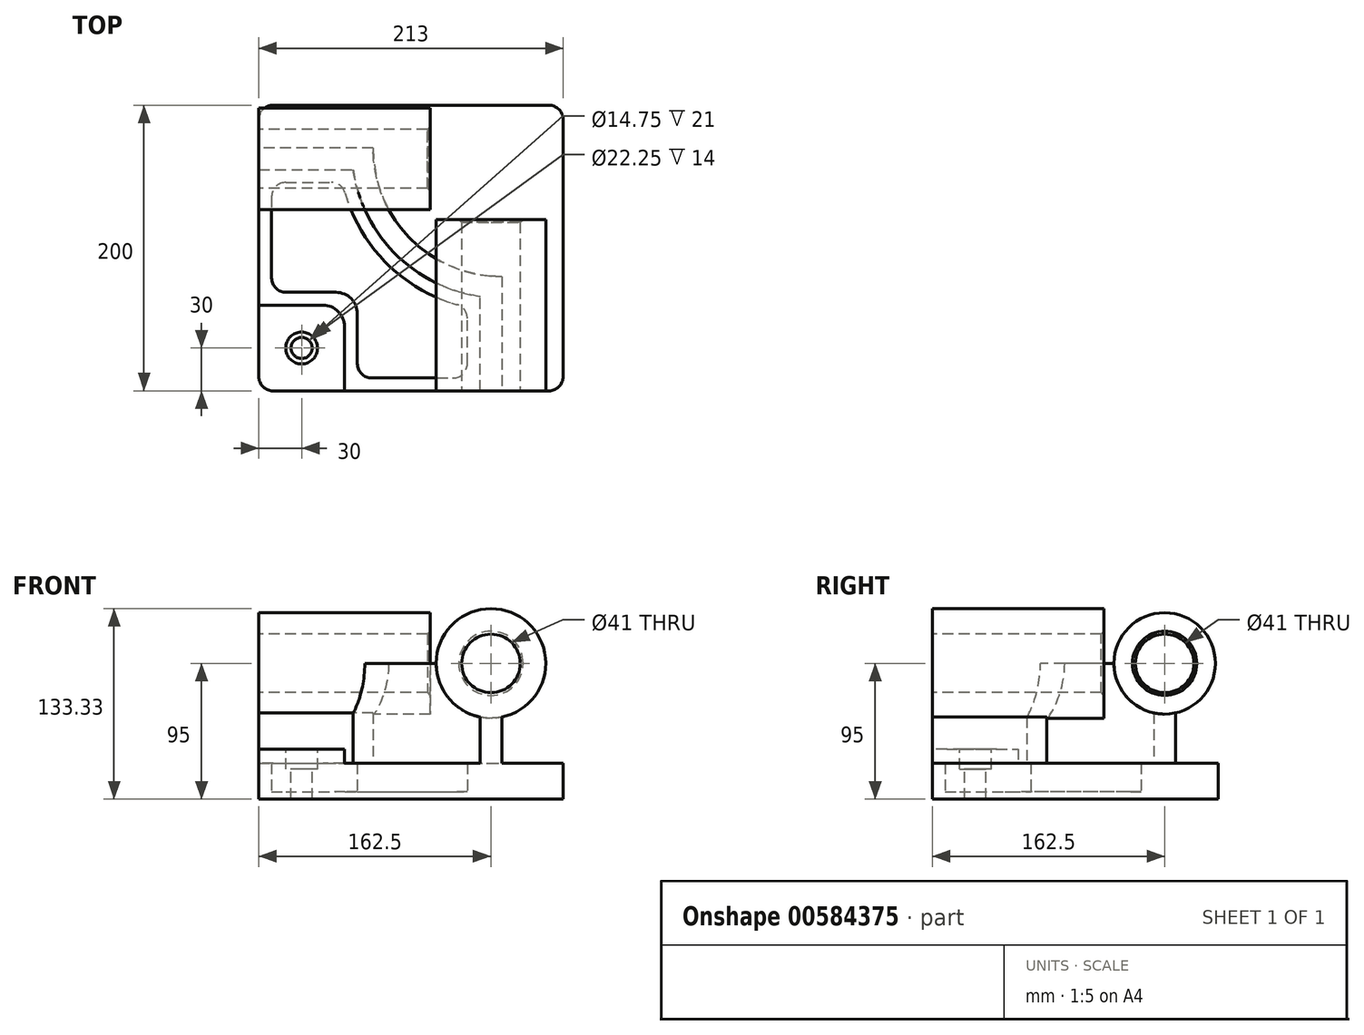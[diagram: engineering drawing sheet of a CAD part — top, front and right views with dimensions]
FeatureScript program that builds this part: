
annotation { "Feature Type Name" : "Feature", "Feature Type Description" : "" }
export const myFeature = defineFeature(function(context is Context, id is Id, definition is map)
    precondition{}
    {
        {
            var Q0;
            Q0=qCreatedBy(makeId("Top.planeOp"),FACE);
            var sketch = newSketch(context, id + "F0", { "sketchPlane" : qUnion([Q0])});
            skLineSegment(sketch, "E0", {"start": v(0, 0) * mm, "end": v(213, 0) * mm});
            skLineSegment(sketch, "E1", {"start": v(0, 0) * mm, "end": v(0, 200) * mm});
            skLineSegment(sketch, "E2", {"start": v(0, 200) * mm, "end": v(213, 200) * mm});
            skLineSegment(sketch, "E3", {"start": v(213, 200) * mm, "end": v(213, 0) * mm});
            skLineSegment(sketch, "E4", {"start": v(0, 170) * mm, "end": v(80, 170) * mm});
            skLineSegment(sketch, "E5", {"start": v(170, 80) * mm, "end": v(170, 0) * mm});
            skLineSegment(sketch, "E6", {"start": v(0, 60) * mm, "end": v(45, 60) * mm});
            skLineSegment(sketch, "E7", {"start": v(60, 45) * mm, "end": v(60, 0) * mm});
            skPoint(sketch, "E8.visualSharp", {"position": v(60, 60) * mm});
            skArc(sketch, "E8.filletArc", {"start": v(60, 45) * mm, "mid": v(55.6, 55.6) * mm, "end": v(45, 60) * mm});
            skArc(sketch, "E9", {"start": v(80, 170) * mm, "mid": v(106.36, 106.36) * mm, "end": v(170, 80) * mm});
            skArc(sketch, "E10", {"start": v(66.08, 155) * mm, "mid": v(95.75, 95.75) * mm, "end": v(155, 66.08) * mm});
            skLineSegment(sketch, "E11", {"start": v(0, 155) * mm, "end": v(66.08, 155) * mm});
            skLineSegment(sketch, "E12", {"start": v(155, 0) * mm, "end": v(155, 66.08) * mm});
            skLineSegment(sketch, "E13", {"start": v(9, 136) * mm, "end": v(9, 79) * mm});
            skLineSegment(sketch, "E14", {"start": v(79, 9) * mm, "end": v(136, 9) * mm});
            skLineSegment(sketch, "E15", {"start": v(19, 146) * mm, "end": v(50.75, 146) * mm});
            skLineSegment(sketch, "E16", {"start": v(146, 19) * mm, "end": v(146, 50.75) * mm});
            skArc(sketch, "E17", {"start": v(60.37, 138.74) * mm, "mid": v(89.39, 89.39) * mm, "end": v(138.74, 60.37) * mm});
            skPoint(sketch, "E18.orphan", {"position": v(66.08, 146) * mm});
            skLineSegment(sketch, "E19", {"start": v(19, 69) * mm, "end": v(54, 69) * mm});
            skLineSegment(sketch, "E20", {"start": v(69, 19) * mm, "end": v(69, 54) * mm});
            skPoint(sketch, "E21.orphan", {"position": v(9, 60) * mm});
            skPoint(sketch, "E22.orphan", {"position": v(60, 9) * mm});
            skPoint(sketch, "E23.visualSharp", {"position": v(9, 146) * mm});
            skArc(sketch, "E23.filletArc", {"start": v(19, 146) * mm, "mid": v(11.93, 143.07) * mm, "end": v(9, 136) * mm});
            skPoint(sketch, "E24.visualSharp", {"position": v(58.55, 146) * mm});
            skArc(sketch, "E24.filletArc", {"start": v(60.37, 138.74) * mm, "mid": v(56.78, 143.98) * mm, "end": v(50.75, 146) * mm});
            skPoint(sketch, "E25.visualSharp", {"position": v(146, 58.55) * mm});
            skArc(sketch, "E25.filletArc", {"start": v(146, 50.75) * mm, "mid": v(143.98, 56.78) * mm, "end": v(138.74, 60.37) * mm});
            skPoint(sketch, "E26.visualSharp", {"position": v(146, 9) * mm});
            skArc(sketch, "E26.filletArc", {"start": v(136, 9) * mm, "mid": v(143.07, 11.93) * mm, "end": v(146, 19) * mm});
            skPoint(sketch, "E27.visualSharp", {"position": v(69, 9) * mm});
            skArc(sketch, "E27.filletArc", {"start": v(69, 19) * mm, "mid": v(71.93, 11.93) * mm, "end": v(79, 9) * mm});
            skPoint(sketch, "E28.visualSharp", {"position": v(69, 69) * mm});
            skArc(sketch, "E28.filletArc", {"start": v(69, 54) * mm, "mid": v(64.6, 64.6) * mm, "end": v(54, 69) * mm});
            skPoint(sketch, "E29.visualSharp", {"position": v(9, 69) * mm});
            skArc(sketch, "E29.filletArc", {"start": v(9, 79) * mm, "mid": v(11.93, 71.93) * mm, "end": v(19, 69) * mm});
            skCircle(sketch, "E30", {"center": v(30, 30) * mm, "radius": 10 * mm});
            skSolve(sketch);
        }
        {
            var Q0;
            {var subQ1=sQuery(id+"F0.wireOp",EDGE,"E6");Q0=makeQuery(id+"F0.imprint","IMPRINT",FACE,{"disambiguationData":[TD([[makeQuery(id+"F0.imprint","IMPRINT",EDGE,{"derivedFrom":subQ1}),-1.0]])]});}
            var Q1;
            Q1=makeQuery(id+"F0.imprint","IMPRINT",FACE,{"disambiguationData":[TD([[makeQuery(id+"F0.imprint","IMPRINT",EDGE,{"derivedFrom":sQuery(id+"F0.wireOp",EDGE,"E30")}),1.0]])]});
            extrude(context, id + "F1", {"entities" : qUnion([Q0, Q1]), "depth" : 35 * mm, "offsetDistance" : 25 * mm});
        }
        {
            var Q0;
            {var subQ2=sQuery(id+"F0.wireOp",EDGE,"E6");Q0=makeQuery(id+"F0.imprint","IMPRINT",FACE,{"disambiguationData":[TD([[makeQuery(id+"F0.imprint","IMPRINT",EDGE,{"derivedFrom":subQ2}),1.0]])]});}
            extrude(context, id + "F2", {"entities" : qUnion([Q0]), "operationType" : NewBodyOperationType.ADD, "depth" : 25 * mm, "offsetDistance" : 25 * mm});
        }
        {
            var Q0;
            {var subQ0=sQuery(id+"F0.wireOp",EDGE,"E4");Q0=makeQuery(id+"F0.imprint","IMPRINT",FACE,{"disambiguationData":[TD([[makeQuery(id+"F0.imprint","IMPRINT",EDGE,{"derivedFrom":subQ0}),-1.0]])]});}
            extrude(context, id + "F3", {"entities" : qUnion([Q0]), "operationType" : NewBodyOperationType.ADD, "depth" : 95 * mm, "offsetDistance" : 25 * mm});
        }
        {
            var Q0;
            Q0=makeQuery(id+"F1.opExtrude","CAP_FACE",FACE,{"disambiguationData":[OSD([sQuery(id+"F0.wireOp",EDGE,"E0"),sQuery(id+"F0.wireOp",EDGE,"E1"),sQuery(id+"F0.wireOp",EDGE,"E6"),sQuery(id+"F0.wireOp",EDGE,"E7"),sQuery(id+"F0.wireOp",EDGE,"E8.filletArc"),sQuery(id+"F0.wireOp",EDGE,"E30")])],"isStart":false});
            var sketch = newSketch(context, id + "F4", { "sketchPlane" : qUnion([Q0])});
            skPoint(sketch, "E31.0", {"position": v(30, 30) * mm});
            skSolve(sketch);
        }
        {
            var Q0;
            {var subQ1=sQuery(id+"F0.wireOp",EDGE,"E2");Q0=makeQuery(id+"F0.imprint","IMPRINT",FACE,{"disambiguationData":[TD([[makeQuery(id+"F0.imprint","IMPRINT",EDGE,{"derivedFrom":subQ1}),-1.0]])]});}
            extrude(context, id + "F5", {"entities" : qUnion([Q0]), "operationType" : NewBodyOperationType.ADD, "depth" : 25 * mm, "offsetDistance" : 25 * mm});
        }
        {
            var Q0;
            {var subQ0=sQuery(id+"F0.wireOp",EDGE,"E0");Q0=makeQuery(id+"F5.boolean.opBoolean","MERGE",FACE,{"derivedFrom":[makeQuery(id+"F3.boolean.opBoolean","MERGE",FACE,{"derivedFrom":[makeQuery(id+"F2.boolean.opBoolean","MERGE",FACE,{"derivedFrom":[makeQuery(id+"F1.opExtrude","SWEPT_FACE",FACE,{"disambiguationData":[OSD([subQ0])]}),makeQuery(id+"F2.opExtrude","SWEPT_FACE",FACE,{"disambiguationData":[OSD([subQ0])]})]}),makeQuery(id+"F3.opExtrude","SWEPT_FACE",FACE,{"disambiguationData":[OSD([subQ0])]})]}),makeQuery(id+"F5.opExtrude","SWEPT_FACE",FACE,{"disambiguationData":[OSD([subQ0])]})]});}
            var sketch = newSketch(context, id + "F6", { "sketchPlane" : qUnion([Q0])});
            skCircle(sketch, "E32", {"center": v(162.5, 95) * mm, "radius": 38.33 * mm});
            skCircle(sketch, "E33", {"center": v(162.5, 95) * mm, "radius": 20.5 * mm});
            skLineSegment(sketch, "E34.0", {"start": v(155, 95) * mm, "end": v(155, 25) * mm});
            skLineSegment(sketch, "E35.0", {"start": v(170, 95) * mm, "end": v(170, 25) * mm});
            skSolve(sketch);
        }
        {
            var Q0;
            {var subQ0=sQuery(id+"F6.wireOp",EDGE,"E32");var subQ1=sQuery(id+"F0.wireOp",EDGE,"E0");var subQ2=makeQuery(id+"F3.opExtrude","SWEPT_EDGE",EDGE,{"disambiguationData":[OSD([subQ1,sQuery(id+"F0.wireOp",EDGE,"E12")])]});var subQ3=makeQuery(id+"F6.imprint","INTERSECT",VERTEX,{"derivedFrom":[subQ2,subQ0]});Q0=makeQuery(id+"F6.imprint","IMPRINT",FACE,{"disambiguationData":[TD([[makeQuery(id+"F6.imprint","IMPRINT",EDGE,{"disambiguationData":[TD([[subQ3,1.0]])],"derivedFrom":subQ0}),1.0]])]});}
            var Q1;
            {var subQ0=sQuery(id+"F6.wireOp",EDGE,"E32");var subQ1=sQuery(id+"F0.wireOp",EDGE,"E0");var subQ2=makeQuery(id+"F3.opExtrude","SWEPT_EDGE",EDGE,{"disambiguationData":[OSD([subQ1,sQuery(id+"F0.wireOp",EDGE,"E12")])]});var subQ3=makeQuery(id+"F6.imprint","INTERSECT",VERTEX,{"derivedFrom":[subQ2,subQ0]});Q1=makeQuery(id+"F6.imprint","IMPRINT",FACE,{"disambiguationData":[TD([[makeQuery(id+"F6.imprint","IMPRINT",EDGE,{"disambiguationData":[TD([[subQ3,-1.0]])],"derivedFrom":subQ0}),1.0]])]});}
            extrude(context, id + "F7", {"entities" : qUnion([Q0, Q1]), "operationType" : NewBodyOperationType.ADD, "oppositeDirection" : true, "depth" : 120 * mm, "offsetDistance" : 25 * mm});
        }
        {
            var Q0;
            {var subQ0=sQuery(id+"F0.wireOp",EDGE,"E1");Q0=makeQuery(id+"F5.boolean.opBoolean","MERGE",FACE,{"derivedFrom":[makeQuery(id+"F3.boolean.opBoolean","MERGE",FACE,{"derivedFrom":[makeQuery(id+"F2.boolean.opBoolean","MERGE",FACE,{"derivedFrom":[makeQuery(id+"F1.opExtrude","SWEPT_FACE",FACE,{"disambiguationData":[OSD([subQ0])]}),makeQuery(id+"F2.opExtrude","SWEPT_FACE",FACE,{"disambiguationData":[OSD([subQ0])]})]}),makeQuery(id+"F3.opExtrude","SWEPT_FACE",FACE,{"disambiguationData":[OSD([subQ0])]})]}),makeQuery(id+"F5.opExtrude","SWEPT_FACE",FACE,{"disambiguationData":[OSD([subQ0])]})]});}
            var sketch = newSketch(context, id + "F8", { "sketchPlane" : qUnion([Q0])});
            skLineSegment(sketch, "E36.0.0", {"start": v(-200, 0) * mm, "end": v(0, 0) * mm});
            skLineSegment(sketch, "E36.0.1", {"start": v(0, 0) * mm, "end": v(0, 35) * mm});
            skLineSegment(sketch, "E36.0.2", {"start": v(0, 35) * mm, "end": v(-60, 35) * mm});
            skLineSegment(sketch, "E36.0.3", {"start": v(-60, 35) * mm, "end": v(-60, 25) * mm});
            skLineSegment(sketch, "E36.0.4", {"start": v(-60, 25) * mm, "end": v(-155, 25) * mm});
            skLineSegment(sketch, "E36.0.5", {"start": v(-155, 25) * mm, "end": v(-155, 95) * mm});
            skLineSegment(sketch, "E36.0.6", {"start": v(-155, 95) * mm, "end": v(-170, 95) * mm});
            skLineSegment(sketch, "E36.0.7", {"start": v(-170, 95) * mm, "end": v(-170, 25) * mm});
            skLineSegment(sketch, "E36.0.8", {"start": v(-170, 25) * mm, "end": v(-200, 25) * mm});
            skLineSegment(sketch, "E36.0.9", {"start": v(-200, 25) * mm, "end": v(-200, 0) * mm});
            skCircle(sketch, "E37", {"center": v(-162.5, 95) * mm, "radius": 20.5 * mm});
            skCircle(sketch, "E38", {"center": v(-162.5, 95) * mm, "radius": 35.5 * mm});
            skSolve(sketch);
        }
        {
            var Q0;
            {var subQ0=sQuery(id+"F8.wireOp",EDGE,"E38");var subQ1=sQuery(id+"F8.wireOp",EDGE,"E36.0.5");var subQ2=makeQuery(id+"F8.imprint","INTERSECT",VERTEX,{"derivedFrom":[subQ1,subQ0]});Q0=makeQuery(id+"F8.imprint","IMPRINT",FACE,{"disambiguationData":[TD([[makeQuery(id+"F8.imprint","IMPRINT",EDGE,{"disambiguationData":[TD([[subQ2,1.0]])],"derivedFrom":subQ1}),1.0]])]});}
            var Q1;
            {var subQ0=sQuery(id+"F8.wireOp",EDGE,"E38");var subQ1=sQuery(id+"F8.wireOp",EDGE,"E36.0.5");var subQ2=makeQuery(id+"F8.imprint","INTERSECT",VERTEX,{"derivedFrom":[subQ1,subQ0]});Q1=makeQuery(id+"F8.imprint","IMPRINT",FACE,{"disambiguationData":[TD([[makeQuery(id+"F8.imprint","IMPRINT",EDGE,{"disambiguationData":[TD([[subQ2,1.0]])],"derivedFrom":subQ1}),-1.0]])]});}
            extrude(context, id + "F9", {"entities" : qUnion([Q0, Q1]), "operationType" : NewBodyOperationType.ADD, "oppositeDirection" : true, "depth" : 120 * mm, "offsetDistance" : 25 * mm});
        }
        {
            var Q0;
            Q0=makeQuery(id+"F1.opExtrude","SWEPT_EDGE",EDGE,{"disambiguationData":[OSD([sQuery(id+"F0.wireOp",EDGE,"E0"),sQuery(id+"F0.wireOp",EDGE,"E1")])]});
            var Q1;
            Q1=makeQuery(id+"F5.opExtrude","SWEPT_EDGE",EDGE,{"disambiguationData":[OSD([sQuery(id+"F0.wireOp",EDGE,"E0"),sQuery(id+"F0.wireOp",EDGE,"E3")])]});
            var Q2;
            Q2=makeQuery(id+"F5.opExtrude","SWEPT_EDGE",EDGE,{"disambiguationData":[OSD([sQuery(id+"F0.wireOp",EDGE,"E2"),sQuery(id+"F0.wireOp",EDGE,"E3")])]});
            var Q3;
            Q3=makeQuery(id+"F5.opExtrude","SWEPT_EDGE",EDGE,{"disambiguationData":[OSD([sQuery(id+"F0.wireOp",EDGE,"E1"),sQuery(id+"F0.wireOp",EDGE,"E2")])]});
            fillet(context, id + "F10", {"entities" : qUnion([Q0, Q1, Q2, Q3]), "radius" : 10 * mm, "tangentPropagation" : true, "allowEdgeOverflow" : false});
        }
        {
            var Q0;
            Q0=sQuery(id+"F8.wireOp",VERTEX,"E37.center");
            var Q1;
            Q1=sQuery(id+"F6.wireOp",VERTEX,"E32.center");
            var Q2;
            Q2=makeQuery(id+"F1.opExtrude","SWEPT_BODY",BODY,{"disambiguationData":[OSD([sQuery(id+"F0.wireOp",EDGE,"E0"),sQuery(id+"F0.wireOp",EDGE,"E1"),sQuery(id+"F0.wireOp",EDGE,"E6"),sQuery(id+"F0.wireOp",EDGE,"E7"),sQuery(id+"F0.wireOp",EDGE,"E8.filletArc")])]});
            hole(context, id + "F11", {"style" : HoleStyle.SIMPLE, "endStyle" : HoleEndStyle.BLIND, "holeDiameter" : 41 * mm, "majorDiameter" : 5 * mm, "holeDepth" : 120 * mm, "isTappedThrough" : true, "tappedDepth" : 54 * mm, "tapClearance" : 3, "locations" : qUnion([Q0, Q1]), "scope" : qUnion([Q2])});
        }
        {
            var Q0;
            Q0=sQuery(id+"F4.wireOp",VERTEX,"E31.0");
            var Q1;
            Q1=makeQuery(id+"F1.opExtrude","SWEPT_BODY",BODY,{"disambiguationData":[OSD([sQuery(id+"F0.wireOp",EDGE,"E0"),sQuery(id+"F0.wireOp",EDGE,"E1"),sQuery(id+"F0.wireOp",EDGE,"E6"),sQuery(id+"F0.wireOp",EDGE,"E7"),sQuery(id+"F0.wireOp",EDGE,"E8.filletArc")])]});
            hole(context, id + "F12", {"style" : HoleStyle.C_BORE, "endStyle" : HoleEndStyle.THROUGH, "standardTappedOrClearance" : lookupTablePath({ "standard" : "ISO", "fit" : "Close", "size" : "M14", "type" : "Clearance" }), "standardBlindInLast" : lookupTablePath({ "fit" : "Close", "standard" : "ISO", "size" : "M14", "type" : "Clearance" }), "holeDiameter" : 14.75 * mm, "cBoreDiameter" : 22.25 * mm, "cBoreDepth" : 14 * mm, "majorDiameter" : 5 * mm, "isTappedThrough" : true, "tappedDepth" : 54 * mm, "tapClearance" : 3, "locations" : qUnion([Q0]), "scope" : qUnion([Q1])});
        }
        {
            var Q0;
            Q0=makeQuery(id+"F7.opExtrude","CAP_EDGE",EDGE,{"disambiguationData":[OSD([sQuery(id+"F6.wireOp",EDGE,"E33")])],"isStart":false});
            var Q1;
            Q1=makeQuery(id+"F11.hole-0.boolean.opBoolean","MERGE",EDGE,{"derivedFrom":[makeQuery(id+"F9.opExtrude","CAP_EDGE",EDGE,{"disambiguationData":[OSD([sQuery(id+"F8.wireOp",EDGE,"E37")])],"isStart":true}),makeQuery(id+"F11.hole-0.opRevolve","SWEPT_EDGE",EDGE,{"disambiguationData":[OSD([sQuery(id+"F11.hole-0.sketch.wireOp",EDGE,"core_line_2"),sQuery(id+"F11.hole-0.sketch.wireOp",EDGE,"core_line_3")])]})]});
            var Q2;
            Q2=makeQuery(id+"F8rdnmnxx8fGRCr_1.hole-0.boolean.opBoolean","MERGE",EDGE,{"derivedFrom":[makeQuery(id+"F7.opExtrude","CAP_EDGE",EDGE,{"disambiguationData":[OSD([sQuery(id+"F6.wireOp",EDGE,"E33")])],"isStart":true}),makeQuery(id+"F8rdnmnxx8fGRCr_1.hole-0.opRevolve","SWEPT_EDGE",EDGE,{"disambiguationData":[OSD([sQuery(id+"F8rdnmnxx8fGRCr_1.hole-0.sketch.wireOp",EDGE,"core_line_2"),sQuery(id+"F8rdnmnxx8fGRCr_1.hole-0.sketch.wireOp",EDGE,"core_line_3")])]})]});
            var Q3;
            Q3=makeQuery(id+"F9.opExtrude","CAP_EDGE",EDGE,{"disambiguationData":[OSD([sQuery(id+"F8.wireOp",EDGE,"E37")])],"isStart":false});
            chamfer(context, id + "F13", {"entities" : qUnion([Q0, Q1, Q2, Q3]), "chamferType" : ChamferType.OFFSET_ANGLE, "width" : 2 * mm, "oppositeDirection" : false, "angle" : 45 * degree, "tangentPropagation" : true});
        }
        {
            var Q0;
            Q0=makeQuery(id+"F0.imprint","IMPRINT",FACE,{"disambiguationData":[TD([[makeQuery(id+"F0.imprint","IMPRINT",EDGE,{"derivedFrom":sQuery(id+"F0.wireOp",EDGE,"E13")}),1.0]])]});
            extrude(context, id + "F14", {"entities" : qUnion([Q0]), "operationType" : NewBodyOperationType.ADD, "depth" : 5 * mm, "offsetDistance" : 25 * mm});
        }
    });
